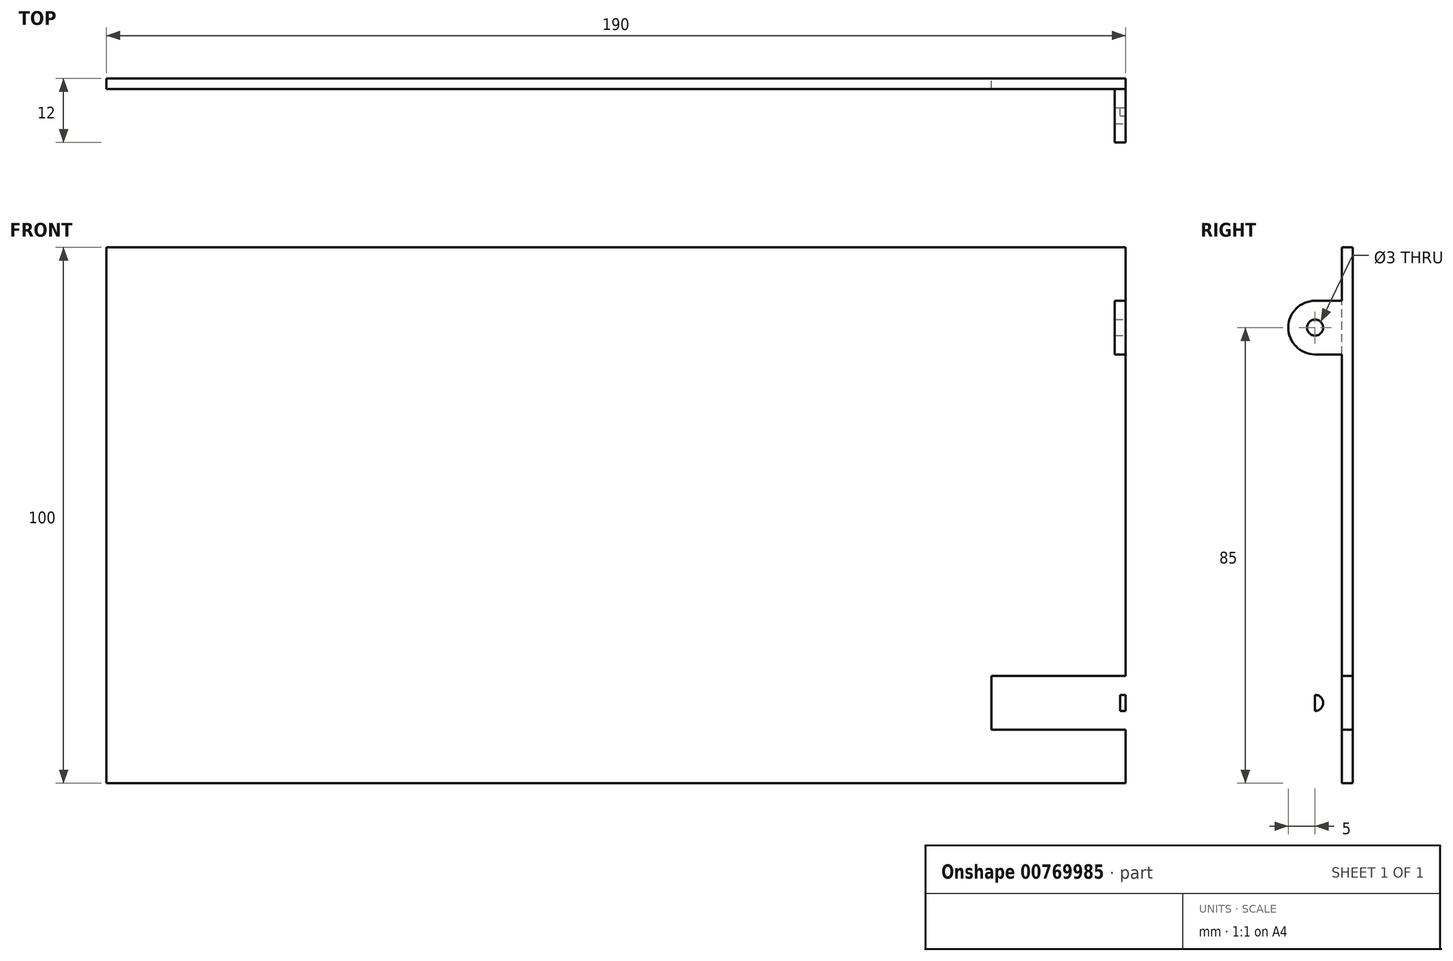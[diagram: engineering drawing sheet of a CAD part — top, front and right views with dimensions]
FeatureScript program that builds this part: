
annotation { "Feature Type Name" : "Feature", "Feature Type Description" : "" }
export const myFeature = defineFeature(function(context is Context, id is Id, definition is map)
    precondition{}
    {
        {
            var Q0;
            Q0=qCreatedBy(makeId("Front.planeOp"),FACE);
            var sketch = newSketch(context, id + "F0", { "sketchPlane" : qUnion([Q0])});
            skLineSegment(sketch, "E0.bottom", {"start": v(95, -50) * mm, "end": v(-95, -50) * mm});
            skLineSegment(sketch, "E0.top", {"start": v(95, 50) * mm, "end": v(-95, 50) * mm});
            skLineSegment(sketch, "E0.left", {"start": v(95, -50) * mm, "end": v(95, 50) * mm});
            skLineSegment(sketch, "E0.right", {"start": v(-95, -50) * mm, "end": v(-95, 50) * mm});
            skPoint(sketch, "E0.middle", {"position": v(0, 0) * mm});
            skLineSegment(sketch, "E1.bottom", {"start": v(95, 40) * mm, "end": v(94, 40) * mm});
            skLineSegment(sketch, "E1.top", {"start": v(95, 30) * mm, "end": v(94, 30) * mm});
            skLineSegment(sketch, "E1.left", {"start": v(95, 40) * mm, "end": v(95, 30) * mm});
            skLineSegment(sketch, "E1.right", {"start": v(94, 40) * mm, "end": v(94, 30) * mm});
            skLineSegment(sketch, "E2.MirrorCS", {"start": v(94, -40) * mm, "end": v(94, -30) * mm});
            skLineSegment(sketch, "E3.MirrorCS", {"start": v(95, -40) * mm, "end": v(95, -30) * mm});
            skLineSegment(sketch, "E4.MirrorCS", {"start": v(95, -30) * mm, "end": v(94, -30) * mm});
            skLineSegment(sketch, "E5.MirrorCS", {"start": v(95, -40) * mm, "end": v(94, -40) * mm});
            skSolve(sketch);
        }
        {
            var Q0;
            {var subQ3=sQuery(id+"F0.wireOp",EDGE,"E0.bottom");Q0=makeQuery(id+"F0.imprint","IMPRINT",FACE,{"disambiguationData":[TD([[makeQuery(id+"F0.imprint","IMPRINT",EDGE,{"derivedFrom":subQ3}),-1.0]])]});}
            extrude(context, id + "F1", {"entities" : qUnion([Q0]), "depth" : 2 * mm, "offsetDistance" : 25 * mm});
        }
        {
            var Q0;
            {var subQ0=sQuery(id+"F0.wireOp",EDGE,"E1.bottom");Q0=makeQuery(id+"F0.imprint","IMPRINT",FACE,{"disambiguationData":[TD([[makeQuery(id+"F0.imprint","IMPRINT",EDGE,{"derivedFrom":subQ0}),1.0]])]});}
            var Q1;
            Q1=makeQuery(id+"F0.imprint","IMPRINT",FACE,{"disambiguationData":[TD([[makeQuery(id+"F0.imprint","IMPRINT",EDGE,{"derivedFrom":sQuery(id+"F0.wireOp",EDGE,"E2.MirrorCS")}),-1.0]])]});
            extrude(context, id + "F2", {"entities" : qUnion([Q0, Q1]), "depth" : 7 * mm, "offsetDistance" : 25 * mm});
        }
        {
            var Q0;
            {var subQ0=sQuery(id+"F0.wireOp",EDGE,"E0.left");Q0=makeQuery(id+"F2.opExtrude","SWEPT_FACE",FACE,{"disambiguationData":[OSD([subQ0]),TDD([makeQuery(id+"F0.imprint","IMPRINT",EDGE,{"disambiguationData":[TD([[makeQuery(id+"F0.imprint","INTERSECT",VERTEX,{"derivedFrom":[subQ0,sQuery(id+"F0.wireOp",EDGE,"E1.bottom")]}),1.0]])],"derivedFrom":subQ0})])]});}
            var sketch = newSketch(context, id + "F3", { "sketchPlane" : qUnion([Q0])});
            skLineSegment(sketch, "E6.bottom", {"start": v(-7, 40) * mm, "end": v(0, 40) * mm});
            skLineSegment(sketch, "E6.top", {"start": v(-7, 30) * mm, "end": v(0, 30) * mm});
            skLineSegment(sketch, "E6.right", {"start": v(0, 40) * mm, "end": v(0, 30) * mm});
            skArc(sketch, "E7", {"start": v(-7, 40) * mm, "mid": v(-12, 35) * mm, "end": v(-7, 30) * mm});
            skCircle(sketch, "E8", {"center": v(-7, 35) * mm, "radius": 1.5 * mm});
            skLineSegment(sketch, "E9.MirrorCS", {"start": v(-7, -30) * mm, "end": v(0, -30) * mm});
            skLineSegment(sketch, "E10.MirrorCS", {"start": v(0, -40) * mm, "end": v(0, -30) * mm});
            skLineSegment(sketch, "E11.MirrorCS", {"start": v(-7, -40) * mm, "end": v(0, -40) * mm});
            skArc(sketch, "E12.MirrorCS", {"start": v(-7, -40) * mm, "mid": v(-12, -35) * mm, "end": v(-7, -30) * mm});
            skCircle(sketch, "E13.MirrorC", {"center": v(-7, -35) * mm, "radius": 1.5 * mm});
            skSolve(sketch);
        }
        {
            var Q0;
            Q0=makeQuery(id+"F3.imprint","IMPRINT",FACE,{"disambiguationData":[TD([[makeQuery(id+"F3.imprint","IMPRINT",EDGE,{"derivedFrom":sQuery(id+"F3.wireOp",EDGE,"E9.MirrorCS")}),-1.0]])]});
            var Q1;
            {var subQ6=sQuery(id+"F3.wireOp",EDGE,"E6.bottom");Q1=makeQuery(id+"F3.imprint","IMPRINT",FACE,{"disambiguationData":[TD([[makeQuery(id+"F3.imprint","IMPRINT",EDGE,{"derivedFrom":subQ6}),-1.0]])]});}
            var Q2;
            Q2=makeQuery(id+"F3.imprint","IMPRINT",FACE,{"disambiguationData":[TD([[makeQuery(id+"F3.imprint","IMPRINT",EDGE,{"derivedFrom":sQuery(id+"F3.wireOp",EDGE,"E13.MirrorC")}),-1.0]])]});
            var Q3;
            {var subQ0=sQuery(id+"F3.wireOp",EDGE,"E7");Q3=makeQuery(id+"F3.imprint","IMPRINT",FACE,{"disambiguationData":[TD([[makeQuery(id+"F3.imprint","IMPRINT",EDGE,{"derivedFrom":subQ0}),1.0]])]});}
            var Q4;
            {var subQ0=sQuery(id+"F3.wireOp",EDGE,"E8");var subQ1=sQuery(id+"F0.wireOp",EDGE,"E0.left");var subQ2=makeQuery(id+"F2.opExtrude","CAP_EDGE",EDGE,{"disambiguationData":[OSD([subQ1]),TDD([makeQuery(id+"F0.imprint","IMPRINT",EDGE,{"disambiguationData":[TD([[makeQuery(id+"F0.imprint","INTERSECT",VERTEX,{"derivedFrom":[subQ1,sQuery(id+"F0.wireOp",EDGE,"E1.bottom")]}),1.0]])],"derivedFrom":subQ1})])],"isStart":false});var subQ3=makeQuery(id+"F3.imprint","INTERSECT",VERTEX,{"disambiguationData":[OD(0.0)],"derivedFrom":[subQ2,subQ0]});Q4=makeQuery(id+"F3.imprint","IMPRINT",FACE,{"disambiguationData":[TD([[makeQuery(id+"F3.imprint","IMPRINT",EDGE,{"disambiguationData":[TD([[subQ3,-1.0]])],"derivedFrom":subQ0}),1.0]])]});}
            var Q5;
            {var subQ0=sQuery(id+"F3.wireOp",EDGE,"E8");var subQ1=sQuery(id+"F0.wireOp",EDGE,"E0.left");var subQ2=makeQuery(id+"F2.opExtrude","CAP_EDGE",EDGE,{"disambiguationData":[OSD([subQ1]),TDD([makeQuery(id+"F0.imprint","IMPRINT",EDGE,{"disambiguationData":[TD([[makeQuery(id+"F0.imprint","INTERSECT",VERTEX,{"derivedFrom":[subQ1,sQuery(id+"F0.wireOp",EDGE,"E1.bottom")]}),1.0]])],"derivedFrom":subQ1})])],"isStart":false});var subQ3=makeQuery(id+"F3.imprint","INTERSECT",VERTEX,{"disambiguationData":[OD(0.0)],"derivedFrom":[subQ2,subQ0]});Q5=makeQuery(id+"F3.imprint","IMPRINT",FACE,{"disambiguationData":[TD([[makeQuery(id+"F3.imprint","IMPRINT",EDGE,{"disambiguationData":[TD([[subQ3,1.0]])],"derivedFrom":subQ0}),1.0]])]});}
            extrude(context, id + "F4", {"entities" : qUnion([Q0, Q1, Q2, Q3, Q4, Q5]), "operationType" : NewBodyOperationType.ADD, "oppositeDirection" : true, "depth" : 2 * mm, "offsetDistance" : 25 * mm});
        }
        {
            var Q0;
            Q0=makeQuery(id+"F3.imprint","IMPRINT",FACE,{"disambiguationData":[TD([[makeQuery(id+"F3.imprint","IMPRINT",EDGE,{"derivedFrom":sQuery(id+"F3.wireOp",EDGE,"E13.MirrorC")}),-1.0]])]});
            var Q1;
            {var subQ0=sQuery(id+"F3.wireOp",EDGE,"E8");var subQ1=sQuery(id+"F0.wireOp",EDGE,"E0.left");var subQ2=makeQuery(id+"F2.opExtrude","CAP_EDGE",EDGE,{"disambiguationData":[OSD([subQ1]),TDD([makeQuery(id+"F0.imprint","IMPRINT",EDGE,{"disambiguationData":[TD([[makeQuery(id+"F0.imprint","INTERSECT",VERTEX,{"derivedFrom":[subQ1,sQuery(id+"F0.wireOp",EDGE,"E1.bottom")]}),1.0]])],"derivedFrom":subQ1})])],"isStart":false});var subQ3=makeQuery(id+"F3.imprint","INTERSECT",VERTEX,{"disambiguationData":[OD(0.0)],"derivedFrom":[subQ2,subQ0]});Q1=makeQuery(id+"F3.imprint","IMPRINT",FACE,{"disambiguationData":[TD([[makeQuery(id+"F3.imprint","IMPRINT",EDGE,{"disambiguationData":[TD([[subQ3,1.0]])],"derivedFrom":subQ0}),1.0]])]});}
            var Q2;
            {var subQ0=sQuery(id+"F3.wireOp",EDGE,"E8");var subQ1=sQuery(id+"F0.wireOp",EDGE,"E0.left");var subQ2=makeQuery(id+"F2.opExtrude","CAP_EDGE",EDGE,{"disambiguationData":[OSD([subQ1]),TDD([makeQuery(id+"F0.imprint","IMPRINT",EDGE,{"disambiguationData":[TD([[makeQuery(id+"F0.imprint","INTERSECT",VERTEX,{"derivedFrom":[subQ1,sQuery(id+"F0.wireOp",EDGE,"E1.bottom")]}),1.0]])],"derivedFrom":subQ1})])],"isStart":false});var subQ3=makeQuery(id+"F3.imprint","INTERSECT",VERTEX,{"disambiguationData":[OD(0.0)],"derivedFrom":[subQ2,subQ0]});Q2=makeQuery(id+"F3.imprint","IMPRINT",FACE,{"disambiguationData":[TD([[makeQuery(id+"F3.imprint","IMPRINT",EDGE,{"disambiguationData":[TD([[subQ3,-1.0]])],"derivedFrom":subQ0}),1.0]])]});}
            extrude(context, id + "F5", {"entities" : qUnion([Q0, Q1, Q2]), "operationType" : NewBodyOperationType.REMOVE, "oppositeDirection" : true, "depth" : 25 * mm, "offsetDistance" : 25 * mm});
        }
    });
